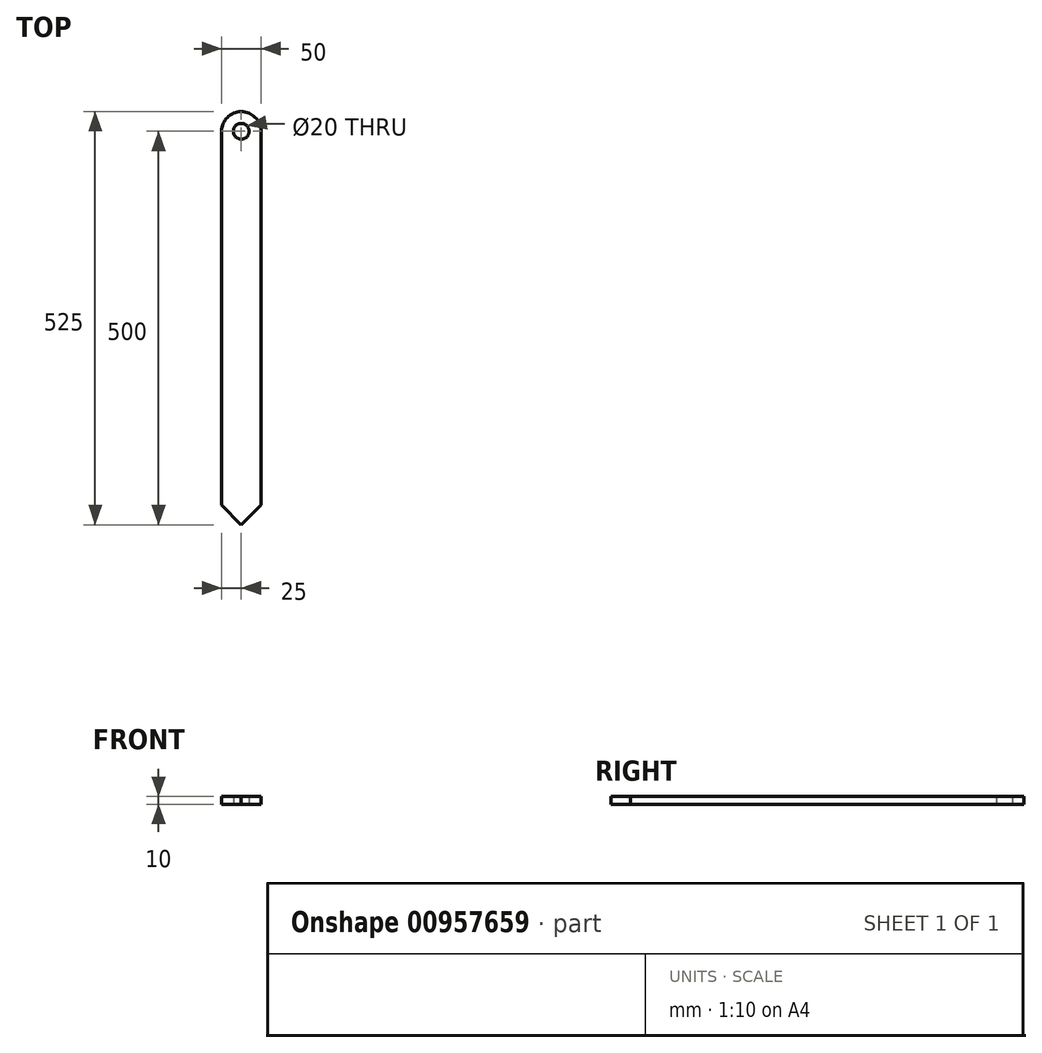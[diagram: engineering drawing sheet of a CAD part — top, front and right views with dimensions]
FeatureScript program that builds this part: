
annotation { "Feature Type Name" : "Feature", "Feature Type Description" : "" }
export const myFeature = defineFeature(function(context is Context, id is Id, definition is map)
    precondition{}
    {
        {
            var Q0;
            Q0=qCreatedBy(makeId("Top.planeOp"),FACE);
            var sketch = newSketch(context, id + "F0", { "sketchPlane" : qUnion([Q0])});
            skLineSegment(sketch, "E0.bottom", {"start": v(0, 0) * mm, "end": v(25, 0) * mm});
            skLineSegment(sketch, "E0.left", {"start": v(0, 0) * mm, "end": v(0, 240) * mm});
            skLineSegment(sketch, "E0.right", {"start": v(25, 0) * mm, "end": v(25, 250) * mm});
            skArc(sketch, "E1", {"start": v(25, 250) * mm, "mid": v(17.68, 267.68) * mm, "end": v(0, 275) * mm});
            skLineSegment(sketch, "E2", {"start": v(0, 275) * mm, "end": v(0, 260) * mm});
            skArc(sketch, "E3", {"start": v(0, 240) * mm, "mid": v(10, 250) * mm, "end": v(0, 260) * mm});
            skSolve(sketch);
        }
        {
            var Q0;
            Q0=qSketchRegion(id+"F0",true);
            extrude(context, id + "F1", {"entities" : qUnion([Q0]), "depth" : 10 * mm, "offsetDistance" : 25.4 * mm});
        }
        {
            var Q0;
            Q0=makeQuery(id+"F1.opExtrude","SWEPT_BODY",BODY,{"disambiguationData":[OSD([sQuery(id+"F0.wireOp",EDGE,"E0.bottom"),sQuery(id+"F0.wireOp",EDGE,"E0.left"),sQuery(id+"F0.wireOp",EDGE,"E0.right"),sQuery(id+"F0.wireOp",EDGE,"E1"),sQuery(id+"F0.wireOp",EDGE,"E2")])]});
            var Q1;
            Q1=makeQuery(id+"F1.opExtrude","SWEPT_FACE",FACE,{"disambiguationData":[OSD([sQuery(id+"F0.wireOp",EDGE,"E0.left"),sQuery(id+"F0.wireOp",EDGE,"E2")])]});
            mirror(context, id + "F2", {"operationType" : NewBodyOperationType.ADD, "entities" : qUnion([Q0]), "mirrorPlane" : qUnion([Q1])});
        }
        {
            var Q0;
            Q0=makeQuery(id+"F1.opExtrude","SWEPT_BODY",BODY,{"disambiguationData":[OSD([sQuery(id+"F0.wireOp",EDGE,"E0.bottom"),sQuery(id+"F0.wireOp",EDGE,"E0.left"),sQuery(id+"F0.wireOp",EDGE,"E0.right"),sQuery(id+"F0.wireOp",EDGE,"E1"),sQuery(id+"F0.wireOp",EDGE,"E2")])]});
            var Q1;
            {var subQ0=makeQuery(id+"F1.opExtrude","SWEPT_FACE",FACE,{"disambiguationData":[OSD([sQuery(id+"F0.wireOp",EDGE,"E0.bottom")])]});Q1=makeQuery(id+"F2.boolean.opBoolean","MERGE",FACE,{"derivedFrom":[subQ0,makeQuery(id+"F2.opPattern","COPY",FACE,{"derivedFrom":subQ0,"instanceName":"1"})]});}
            mirror(context, id + "F3", {"operationType" : NewBodyOperationType.ADD, "entities" : qUnion([Q0]), "mirrorPlane" : qUnion([Q1])});
        }
        {
            var Q0;
            Q0=qCreatedBy(makeId("Top.planeOp"),FACE);
            var sketch = newSketch(context, id + "F4", { "sketchPlane" : qUnion([Q0])});
            skLineSegment(sketch, "E4", {"start": v(0, -250) * mm, "end": v(50, -200) * mm});
            skLineSegment(sketch, "E5", {"start": v(50, -200) * mm, "end": v(50, -344.78) * mm});
            skLineSegment(sketch, "E6", {"start": v(50, -344.78) * mm, "end": v(-50, -344.78) * mm});
            skLineSegment(sketch, "E7", {"start": v(-50, -344.78) * mm, "end": v(-50, -200) * mm});
            skLineSegment(sketch, "E8", {"start": v(-50, -200) * mm, "end": v(0, -250) * mm});
            skSolve(sketch);
        }
        {
            var Q0;
            Q0=makeQuery(id+"F4.imprint","IMPRINT",FACE,{"disambiguationData":[TD([[makeQuery(id+"F4.imprint","IMPRINT",EDGE,{"derivedFrom":sQuery(id+"F4.wireOp",EDGE,"E4")}),-1.0]])]});
            extrude(context, id + "F5", {"entities" : qUnion([Q0]), "operationType" : NewBodyOperationType.REMOVE, "endBound" : BoundingType.THROUGH_ALL, "depth" : 25 * mm, "offsetDistance" : 25 * mm});
        }
        {
            var Q0;
            {var subQ0=makeQuery(id+"F1.opExtrude","CAP_FACE",FACE,{"disambiguationData":[OSD([sQuery(id+"F0.wireOp",EDGE,"E0.bottom"),sQuery(id+"F0.wireOp",EDGE,"E0.left"),sQuery(id+"F0.wireOp",EDGE,"E0.right"),sQuery(id+"F0.wireOp",EDGE,"E1"),sQuery(id+"F0.wireOp",EDGE,"E2"),sQuery(id+"F0.wireOp",EDGE,"E3")])],"isStart":false});var subQ1=makeQuery(id+"F2.boolean.opBoolean","MERGE",FACE,{"derivedFrom":[subQ0,makeQuery(id+"F2.opPattern","COPY",FACE,{"derivedFrom":subQ0,"instanceName":"1"})]});Q0=makeQuery(id+"F3.boolean.opBoolean","MERGE",FACE,{"derivedFrom":[subQ1,makeQuery(id+"F3.opPattern","COPY",FACE,{"derivedFrom":subQ1,"instanceName":"1"})]});}
            var sketch = newSketch(context, id + "F6", { "sketchPlane" : qUnion([Q0])});
            skLineSegment(sketch, "E9", {"start": v(-11.02, -238.98) * mm, "end": v(0, -250) * mm});
            skLineSegment(sketch, "E10", {"start": v(0, -250) * mm, "end": v(11.91, -238.09) * mm});
            skLineSegment(sketch, "E11", {"start": v(11.91, -238.09) * mm, "end": v(-11.02, -238.98) * mm});
            skSolve(sketch);
        }
        {
            var Q0;
            Q0 = qSketchRegion(id + "F6", true);
            var Q1;
            {var subQ0=makeQuery(id+"F1.opExtrude","CAP_FACE",FACE,{"disambiguationData":[OSD([sQuery(id+"F0.wireOp",EDGE,"E0.bottom"),sQuery(id+"F0.wireOp",EDGE,"E0.left"),sQuery(id+"F0.wireOp",EDGE,"E0.right"),sQuery(id+"F0.wireOp",EDGE,"E1"),sQuery(id+"F0.wireOp",EDGE,"E2"),sQuery(id+"F0.wireOp",EDGE,"E3")])],"isStart":true});var subQ1=makeQuery(id+"F2.boolean.opBoolean","MERGE",FACE,{"derivedFrom":[subQ0,makeQuery(id+"F2.opPattern","COPY",FACE,{"derivedFrom":subQ0,"instanceName":"1"})]});Q1=makeQuery(id+"F3.boolean.opBoolean","MERGE",FACE,{"derivedFrom":[subQ1,makeQuery(id+"F3.opPattern","COPY",FACE,{"derivedFrom":subQ1,"instanceName":"1"})]});}
            extrude(context, id + "F7", {"entities" : qUnion([Q0]), "operationType" : NewBodyOperationType.ADD, "endBound" : BoundingType.UP_TO_SURFACE, "oppositeDirection" : true, "depth" : 25 * mm, "endBoundEntityFace" : qUnion([Q1]), "offsetDistance" : 25 * mm});
        }
    });
